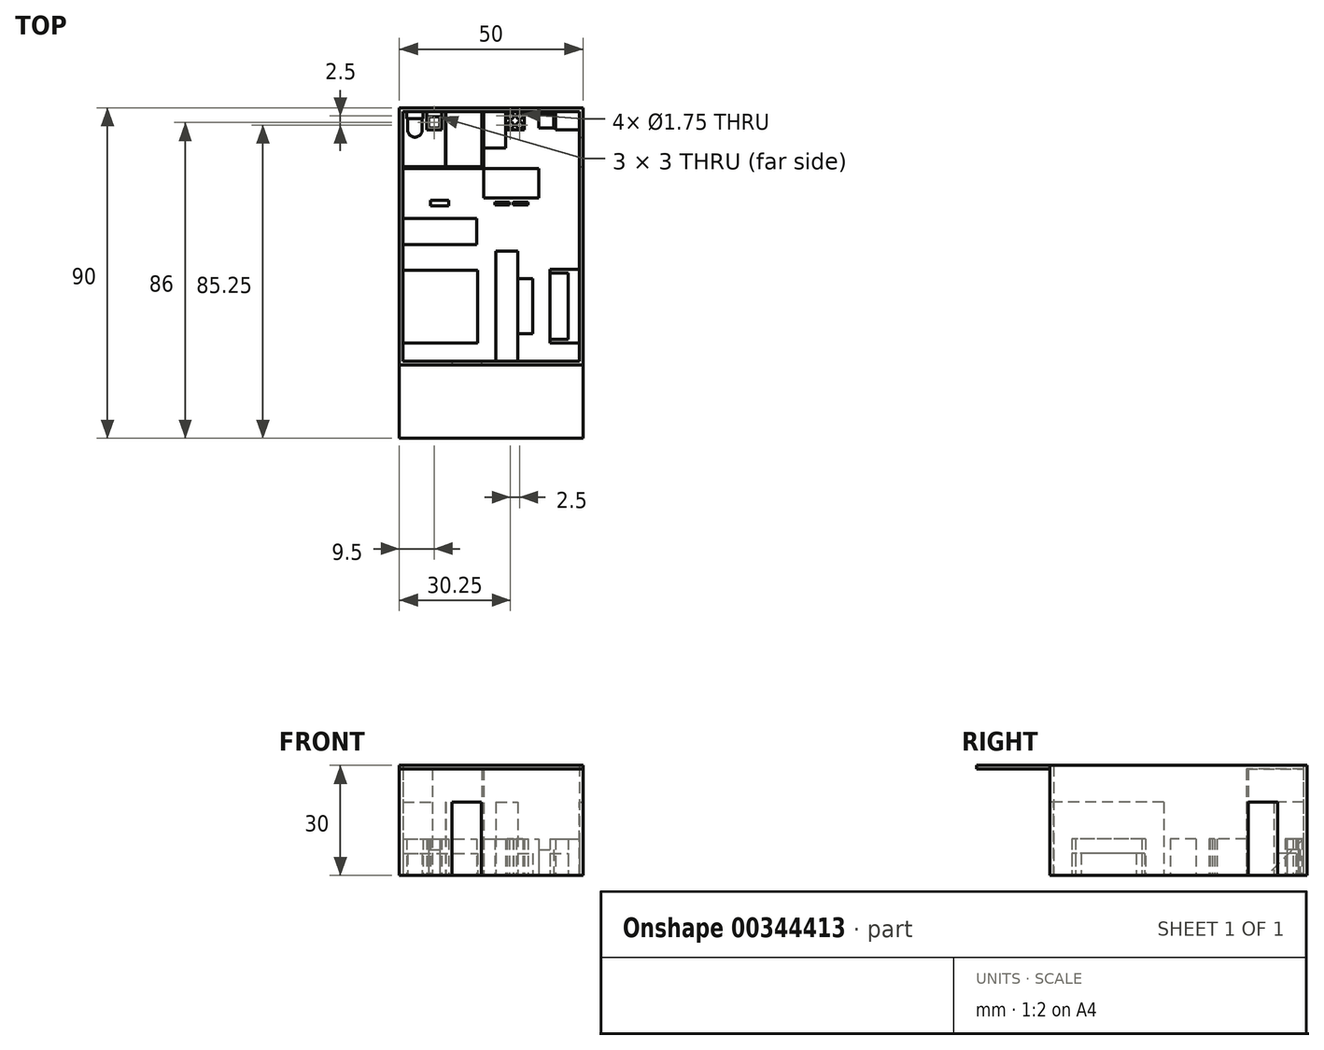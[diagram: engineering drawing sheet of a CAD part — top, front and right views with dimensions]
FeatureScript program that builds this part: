
annotation { "Feature Type Name" : "Feature", "Feature Type Description" : "" }
export const myFeature = defineFeature(function(context is Context, id is Id, definition is map)
    precondition{}
    {
        {
            var Q0;
            Q0=qCreatedBy(makeId("Top.planeOp"),FACE);
            var sketch = newSketch(context, id + "F0", { "sketchPlane" : qUnion([Q0])});
            skLineSegment(sketch, "E0.bottom", {"start": v(-25, 35) * mm, "end": v(25, 35) * mm});
            skLineSegment(sketch, "E0.top", {"start": v(-25, -35) * mm, "end": v(25, -35) * mm});
            skLineSegment(sketch, "E0.left", {"start": v(-25, 35) * mm, "end": v(-25, -35) * mm});
            skLineSegment(sketch, "E0.right", {"start": v(25, 35) * mm, "end": v(25, -35) * mm});
            skLineSegment(sketch, "E1", {"start": v(-25, 0) * mm, "end": v(25, 0) * mm, "construction": true});
            skLineSegment(sketch, "E2", {"start": v(0, 35) * mm, "end": v(0, -35) * mm, "construction": true});
            skLineSegment(sketch, "E3", {"start": v(25, 35) * mm, "end": v(0, 0) * mm, "construction": true});
            skSolve(sketch);
        }
        {
            var Q0;
            Q0=makeQuery(id+"F0.imprint","IMPRINT",FACE,{"disambiguationData":[TD([[makeQuery(id+"F0.imprint","IMPRINT",EDGE,{"derivedFrom":sQuery(id+"F0.wireOp",EDGE,"E0.bottom")}),-1.0]])]});
            extrude(context, id + "F1", {"entities" : qUnion([Q0]), "depth" : 30 * mm});
        }
        {
            var Q0;
            Q0=makeQuery(id+"F1.opExtrude","CAP_FACE",FACE,{"disambiguationData":[OSD([sQuery(id+"F0.wireOp",EDGE,"E0.bottom"),sQuery(id+"F0.wireOp",EDGE,"E0.top"),sQuery(id+"F0.wireOp",EDGE,"E0.left"),sQuery(id+"F0.wireOp",EDGE,"E0.right")])],"isStart":false});
            var Q1;
            Q1=makeQuery(id+"F1.opExtrude","CAP_FACE",FACE,{"disambiguationData":[OSD([sQuery(id+"F0.wireOp",EDGE,"E0.bottom"),sQuery(id+"F0.wireOp",EDGE,"E0.top"),sQuery(id+"F0.wireOp",EDGE,"E0.left"),sQuery(id+"F0.wireOp",EDGE,"E0.right")])],"isStart":true});
            shell(context, id + "F2", {"entities" : qUnion([Q0, Q1]), "thickness" : 1 * mm});
        }
        {
            var Q0;
            Q0=qCreatedBy(makeId("Top.planeOp"),FACE);
            var sketch = newSketch(context, id + "F3", { "sketchPlane" : qUnion([Q0])});
            skLineSegment(sketch, "E4.right", {"start": v(4, 34) * mm, "end": v(4, 29) * mm});
            skLineSegment(sketch, "E5.bottom", {"start": v(4, 34) * mm, "end": v(9, 34) * mm});
            skLineSegment(sketch, "E5.top", {"start": v(4, 29) * mm, "end": v(9, 29) * mm});
            skLineSegment(sketch, "E5.right", {"start": v(9, 34) * mm, "end": v(9, 29) * mm});
            skLineSegment(sketch, "E6.bottom", {"start": v(16, -9) * mm, "end": v(24, -9) * mm});
            skLineSegment(sketch, "E6.top", {"start": v(16, -29) * mm, "end": v(24, -29) * mm});
            skLineSegment(sketch, "E6.left", {"start": v(16, -9) * mm, "end": v(16, -29) * mm});
            skLineSegment(sketch, "E6.right", {"start": v(24, -9) * mm, "end": v(24, -29) * mm});
            skLineSegment(sketch, "E7.bottom", {"start": v(16, -10) * mm, "end": v(21, -10) * mm});
            skLineSegment(sketch, "E7.top", {"start": v(16, -28) * mm, "end": v(21, -28) * mm});
            skLineSegment(sketch, "E7.left", {"start": v(16, -10) * mm, "end": v(16, -28) * mm});
            skLineSegment(sketch, "E7.right", {"start": v(21, -10) * mm, "end": v(21, -28) * mm});
            skLineSegment(sketch, "E8.bottom", {"start": v(7.3, -11.5) * mm, "end": v(11.3, -11.5) * mm});
            skLineSegment(sketch, "E8.top", {"start": v(7.3, -26.5) * mm, "end": v(11.3, -26.5) * mm});
            skLineSegment(sketch, "E8.left", {"start": v(7.3, -11.5) * mm, "end": v(7.3, -26.5) * mm});
            skLineSegment(sketch, "E8.right", {"start": v(11.3, -11.5) * mm, "end": v(11.3, -26.5) * mm});
            skLineSegment(sketch, "E9.bottom", {"start": v(1.3, -4) * mm, "end": v(7.3, -4) * mm});
            skLineSegment(sketch, "E9.top", {"start": v(1.3, -34) * mm, "end": v(7.3, -34) * mm});
            skLineSegment(sketch, "E9.left", {"start": v(1.3, -4) * mm, "end": v(1.3, -34) * mm});
            skLineSegment(sketch, "E9.right", {"start": v(7.3, -4) * mm, "end": v(7.3, -34) * mm});
            skLineSegment(sketch, "E10.bottom", {"start": v(-24, -9.2) * mm, "end": v(-3.7, -9.2) * mm});
            skLineSegment(sketch, "E10.top", {"start": v(-24, -29) * mm, "end": v(-3.7, -29) * mm});
            skLineSegment(sketch, "E10.left", {"start": v(-24, -9.2) * mm, "end": v(-24, -29) * mm});
            skLineSegment(sketch, "E10.right", {"start": v(-3.7, -9.2) * mm, "end": v(-3.7, -29) * mm});
            skLineSegment(sketch, "E11.bottom", {"start": v(-24, 4.8) * mm, "end": v(-4, 4.8) * mm});
            skLineSegment(sketch, "E11.top", {"start": v(-24, -2.2) * mm, "end": v(-4, -2.2) * mm});
            skLineSegment(sketch, "E11.left", {"start": v(-24, 4.8) * mm, "end": v(-24, -2.2) * mm});
            skLineSegment(sketch, "E11.right", {"start": v(-4, 4.8) * mm, "end": v(-4, -2.2) * mm});
            skLineSegment(sketch, "E12.bottom", {"start": v(-16.5, 9.8) * mm, "end": v(-11.5, 9.8) * mm});
            skLineSegment(sketch, "E12.top", {"start": v(-16.5, 4.8) * mm, "end": v(-11.5, 4.8) * mm});
            skLineSegment(sketch, "E12.left", {"start": v(-16.5, 9.8) * mm, "end": v(-16.5, 4.8) * mm});
            skLineSegment(sketch, "E12.right", {"start": v(-11.5, 9.8) * mm, "end": v(-11.5, 4.8) * mm});
            skLineSegment(sketch, "E13.bottom", {"start": v(-24, -29) * mm, "end": v(-19, -29) * mm});
            skLineSegment(sketch, "E13.top", {"start": v(-24, -34) * mm, "end": v(-19, -34) * mm});
            skLineSegment(sketch, "E13.left", {"start": v(-24, -29) * mm, "end": v(-24, -34) * mm});
            skLineSegment(sketch, "E13.right", {"start": v(-19, -29) * mm, "end": v(-19, -34) * mm});
            skLineSegment(sketch, "E14", {"start": v(-16.5, 8.3) * mm, "end": v(-11.5, 8.3) * mm});
            skLineSegment(sketch, "E15", {"start": v(-14, 4.8) * mm, "end": v(-14, 9.8) * mm, "construction": true});
            skLineSegment(sketch, "E16", {"start": v(-14, -2.2) * mm, "end": v(-14, 4.8) * mm, "construction": true});
            skLineSegment(sketch, "E17.top", {"start": v(-23, 32) * mm, "end": v(-18.5, 32) * mm});
            skLineSegment(sketch, "E17.left", {"start": v(-23, 34) * mm, "end": v(-23, 32) * mm});
            skLineSegment(sketch, "E17.right", {"start": v(-18.5, 34) * mm, "end": v(-18.5, 32) * mm});
            skLineSegment(sketch, "E18", {"start": v(-22.75, 32) * mm, "end": v(-22.75, 29) * mm});
            skLineSegment(sketch, "E19", {"start": v(-18.75, 32) * mm, "end": v(-18.75, 29) * mm});
            skLineSegment(sketch, "E20", {"start": v(-22.75, 29) * mm, "end": v(-18.75, 29) * mm, "construction": true});
            skArc(sketch, "E21", {"start": v(-22.75, 29) * mm, "mid": v(-20.75, 27) * mm, "end": v(-18.75, 29) * mm});
            skLineSegment(sketch, "E22.top", {"start": v(-17.5, 29) * mm, "end": v(-13.5, 29) * mm});
            skLineSegment(sketch, "E22.left", {"start": v(-17.5, 34) * mm, "end": v(-17.5, 29) * mm});
            skLineSegment(sketch, "E22.right", {"start": v(-13.5, 34) * mm, "end": v(-13.5, 29) * mm});
            skLineSegment(sketch, "E23.bottom", {"start": v(-17, 32.5) * mm, "end": v(-14, 32.5) * mm});
            skLineSegment(sketch, "E23.top", {"start": v(-17, 29.5) * mm, "end": v(-14, 29.5) * mm});
            skLineSegment(sketch, "E23.left", {"start": v(-17, 32.5) * mm, "end": v(-17, 29.5) * mm});
            skLineSegment(sketch, "E23.right", {"start": v(-14, 32.5) * mm, "end": v(-14, 29.5) * mm});
            skLineSegment(sketch, "E24.bottom", {"start": v(-12.5, 34) * mm, "end": v(-2.5, 34) * mm});
            skLineSegment(sketch, "E24.top", {"start": v(-12.5, 19) * mm, "end": v(-2.5, 19) * mm});
            skLineSegment(sketch, "E24.left", {"start": v(-12.5, 34) * mm, "end": v(-12.5, 19) * mm});
            skLineSegment(sketch, "E24.right", {"start": v(-2.5, 34) * mm, "end": v(-2.5, 19) * mm});
            skLineSegment(sketch, "E25", {"start": v(-24, 19) * mm, "end": v(-2.5, 19) * mm});
            skLineSegment(sketch, "E26", {"start": v(-24, 18.5) * mm, "end": v(-2, 18.5) * mm});
            skLineSegment(sketch, "E27", {"start": v(-2, 18.5) * mm, "end": v(-2, 34) * mm});
            skLineSegment(sketch, "E28", {"start": v(-16, 19) * mm, "end": v(-16, 18.5) * mm});
            skLineSegment(sketch, "E29", {"start": v(-23, 34) * mm, "end": v(-18.5, 34) * mm});
            skLineSegment(sketch, "E30", {"start": v(-17.5, 34) * mm, "end": v(-13.5, 34) * mm});
            skLineSegment(sketch, "E31", {"start": v(-24, 19) * mm, "end": v(-24, 18.5) * mm});
            skLineSegment(sketch, "E32", {"start": v(-2.5, 34) * mm, "end": v(-2, 34) * mm});
            skLineSegment(sketch, "E33", {"start": v(1.3, -19) * mm, "end": v(24, -19) * mm, "construction": true});
            skPoint(sketch, "E33.endSnap0", {"position": v(7.3, -19) * mm});
            skLineSegment(sketch, "E34", {"start": v(24, -19) * mm, "end": v(16, -19) * mm, "construction": true});
            skLineSegment(sketch, "E35", {"start": v(7.3, -19) * mm, "end": v(11.3, -19) * mm, "construction": true});
            skLineSegment(sketch, "E36", {"start": v(6.5, 34) * mm, "end": v(6.5, 29) * mm, "construction": true});
            skLineSegment(sketch, "E37", {"start": v(6.5, 29) * mm, "end": v(4, 31.5) * mm, "construction": true});
            skLineSegment(sketch, "E38", {"start": v(4, 31.5) * mm, "end": v(6.5, 34) * mm, "construction": true});
            skLineSegment(sketch, "E39", {"start": v(4, 31.5) * mm, "end": v(9, 31.5) * mm, "construction": true});
            skLineSegment(sketch, "E40", {"start": v(9, 31.5) * mm, "end": v(6.5, 29) * mm, "construction": true});
            skLineSegment(sketch, "E41", {"start": v(6.5, 34) * mm, "end": v(9, 31.5) * mm, "construction": true});
            skLineSegment(sketch, "E42", {"start": v(4, 34) * mm, "end": v(9, 29) * mm, "construction": true});
            skLineSegment(sketch, "E43", {"start": v(9, 34) * mm, "end": v(4, 29) * mm, "construction": true});
            skCircle(sketch, "E44", {"center": v(5.25, 32.75) * mm, "radius": 0.87 * mm});
            skCircle(sketch, "E45", {"center": v(7.75, 32.75) * mm, "radius": 0.88 * mm});
            skCircle(sketch, "E46", {"center": v(5.25, 30.25) * mm, "radius": 0.88 * mm});
            skCircle(sketch, "E47", {"center": v(7.75, 30.25) * mm, "radius": 0.88 * mm});
            skLineSegment(sketch, "E48.bottom", {"start": v(-2, 34) * mm, "end": v(4, 34) * mm});
            skLineSegment(sketch, "E48.top", {"start": v(-2, 24) * mm, "end": v(4, 24) * mm});
            skLineSegment(sketch, "E48.left", {"start": v(-2, 34) * mm, "end": v(-2, 24) * mm});
            skLineSegment(sketch, "E48.right", {"start": v(4, 34) * mm, "end": v(4, 24) * mm});
            skLineSegment(sketch, "E49.bottom", {"start": v(9, 34) * mm, "end": v(24, 34) * mm});
            skLineSegment(sketch, "E49.top", {"start": v(9, 29) * mm, "end": v(24, 29) * mm});
            skLineSegment(sketch, "E49.right", {"start": v(24, 34) * mm, "end": v(24, 29) * mm});
            skLineSegment(sketch, "E50.bottom", {"start": v(13, 33) * mm, "end": v(17, 33) * mm});
            skLineSegment(sketch, "E50.top", {"start": v(13, 29.5) * mm, "end": v(17, 29.5) * mm});
            skLineSegment(sketch, "E50.left", {"start": v(13, 33) * mm, "end": v(13, 29.5) * mm});
            skLineSegment(sketch, "E50.right", {"start": v(17, 33) * mm, "end": v(17, 29.5) * mm});
            skLineSegment(sketch, "E51.bottom", {"start": v(24, 34) * mm, "end": v(17.5, 34) * mm});
            skLineSegment(sketch, "E51.top", {"start": v(24, 29) * mm, "end": v(17.5, 29) * mm});
            skLineSegment(sketch, "E51.right", {"start": v(17.5, 34) * mm, "end": v(17.5, 29) * mm});
            skLineSegment(sketch, "E52.bottom", {"start": v(-2, 18.5) * mm, "end": v(13, 18.5) * mm});
            skLineSegment(sketch, "E52.top", {"start": v(-2, 10.5) * mm, "end": v(13, 10.5) * mm});
            skLineSegment(sketch, "E52.left", {"start": v(-2, 18.5) * mm, "end": v(-2, 10.5) * mm});
            skLineSegment(sketch, "E52.right", {"start": v(13, 18.5) * mm, "end": v(13, 10.5) * mm});
            skLineSegment(sketch, "E53.bottom", {"start": v(1, 10.5) * mm, "end": v(5, 10.5) * mm});
            skLineSegment(sketch, "E53.top", {"start": v(1, 8.5) * mm, "end": v(5, 8.5) * mm});
            skLineSegment(sketch, "E53.left", {"start": v(1, 10.5) * mm, "end": v(1, 8.5) * mm});
            skLineSegment(sketch, "E53.right", {"start": v(5, 10.5) * mm, "end": v(5, 8.5) * mm});
            skLineSegment(sketch, "E54.bottom", {"start": v(6, 10.5) * mm, "end": v(10, 10.5) * mm});
            skLineSegment(sketch, "E54.top", {"start": v(6, 8.5) * mm, "end": v(10, 8.5) * mm});
            skLineSegment(sketch, "E54.left", {"start": v(6, 10.5) * mm, "end": v(6, 8.5) * mm});
            skLineSegment(sketch, "E54.right", {"start": v(10, 10.5) * mm, "end": v(10, 8.5) * mm});
            skLineSegment(sketch, "E55", {"start": v(1, 9.25) * mm, "end": v(5, 9.25) * mm});
            skLineSegment(sketch, "E56", {"start": v(6, 9.25) * mm, "end": v(10, 9.25) * mm});
            skLineSegment(sketch, "E57", {"start": v(-12.3, 34) * mm, "end": v(-12.3, 19) * mm});
            skLineSegment(sketch, "E58", {"start": v(-12.5, 26) * mm, "end": v(-12.3, 26) * mm});
            skSolve(sketch);
        }
        {
            var Q0;
            Q0=makeQuery(id+"F3.imprint","IMPRINT",FACE,{"disambiguationData":[TD([[makeQuery(id+"F3.imprint","IMPRINT",EDGE,{"derivedFrom":sQuery(id+"F3.wireOp",EDGE,"E22.top")}),1.0]])]});
            var Q1;
            {var subQ0=sQuery(id+"F3.wireOp",EDGE,"E17.left");Q1=makeQuery(id+"F3.imprint","IMPRINT",FACE,{"disambiguationData":[TD([[makeQuery(id+"F3.imprint","IMPRINT",EDGE,{"derivedFrom":subQ0}),1.0]])]});}
            var Q2;
            Q2=makeQuery(id+"F3.imprint","IMPRINT",FACE,{"disambiguationData":[TD([[makeQuery(id+"F3.imprint","IMPRINT",EDGE,{"derivedFrom":sQuery(id+"F3.wireOp",EDGE,"E52.bottom")}),-1.0]])]});
            var Q3;
            {var subQ0=sQuery(id+"F3.wireOp",EDGE,"E53.top");Q3=makeQuery(id+"F3.imprint","IMPRINT",FACE,{"disambiguationData":[TD([[makeQuery(id+"F3.imprint","IMPRINT",EDGE,{"derivedFrom":subQ0}),1.0]])]});}
            var Q4;
            {var subQ0=sQuery(id+"F3.wireOp",EDGE,"E54.top");Q4=makeQuery(id+"F3.imprint","IMPRINT",FACE,{"disambiguationData":[TD([[makeQuery(id+"F3.imprint","IMPRINT",EDGE,{"derivedFrom":subQ0}),1.0]])]});}
            var Q5;
            {var subQ0=sQuery(id+"F3.wireOp",EDGE,"E12.bottom");Q5=makeQuery(id+"F3.imprint","IMPRINT",FACE,{"disambiguationData":[TD([[makeQuery(id+"F3.imprint","IMPRINT",EDGE,{"derivedFrom":subQ0}),-1.0]])]});}
            var Q6;
            Q6=makeQuery(id+"F3.imprint","IMPRINT",FACE,{"disambiguationData":[TD([[makeQuery(id+"F3.imprint","IMPRINT",EDGE,{"derivedFrom":sQuery(id+"F3.wireOp",EDGE,"E11.top")}),1.0]])]});
            var Q7;
            Q7=makeQuery(id+"F3.imprint","IMPRINT",FACE,{"disambiguationData":[TD([[makeQuery(id+"F3.imprint","IMPRINT",EDGE,{"derivedFrom":sQuery(id+"F3.wireOp",EDGE,"E49.bottom")}),-1.0]])]});
            var Q8;
            Q8=makeQuery(id+"F3.imprint","IMPRINT",FACE,{"disambiguationData":[TD([[makeQuery(id+"F3.imprint","IMPRINT",EDGE,{"derivedFrom":sQuery(id+"F3.wireOp",EDGE,"E13.bottom")}),-1.0]])]});
            var Q9;
            {var subQ4=sQuery(id+"F3.wireOp",EDGE,"E6.bottom");Q9=makeQuery(id+"F3.imprint","IMPRINT",FACE,{"disambiguationData":[TD([[makeQuery(id+"F3.imprint","IMPRINT",EDGE,{"derivedFrom":subQ4}),-1.0]])]});}
            var Q10;
            {var subQ1=sQuery(id+"F3.wireOp",EDGE,"E5.bottom");Q10=makeQuery(id+"F3.imprint","IMPRINT",FACE,{"disambiguationData":[TD([[makeQuery(id+"F3.imprint","IMPRINT",EDGE,{"derivedFrom":subQ1}),-1.0]])]});}
            extrude(context, id + "F4", {"entities" : qUnion([Q0, Q1, Q2, Q3, Q4, Q5, Q6, Q7, Q8, Q9, Q10]), "operationType" : NewBodyOperationType.ADD, "depth" : 10 * mm});
        }
        {
            var Q0;
            {var subQ0=sQuery(id+"F3.wireOp",EDGE,"E12.top");Q0=makeQuery(id+"F3.imprint","IMPRINT",FACE,{"disambiguationData":[TD([[makeQuery(id+"F3.imprint","IMPRINT",EDGE,{"derivedFrom":subQ0}),1.0]])]});}
            var Q1;
            {var subQ0=sQuery(id+"F3.wireOp",EDGE,"E53.bottom");Q1=makeQuery(id+"F3.imprint","IMPRINT",FACE,{"disambiguationData":[TD([[makeQuery(id+"F3.imprint","IMPRINT",EDGE,{"derivedFrom":subQ0}),-1.0]])]});}
            var Q2;
            {var subQ0=sQuery(id+"F3.wireOp",EDGE,"E54.bottom");Q2=makeQuery(id+"F3.imprint","IMPRINT",FACE,{"disambiguationData":[TD([[makeQuery(id+"F3.imprint","IMPRINT",EDGE,{"derivedFrom":subQ0}),-1.0]])]});}
            var Q3;
            Q3=makeQuery(id+"F3.imprint","IMPRINT",FACE,{"disambiguationData":[TD([[makeQuery(id+"F3.imprint","IMPRINT",EDGE,{"derivedFrom":sQuery(id+"F3.wireOp",EDGE,"E7.bottom")}),-1.0]])]});
            var Q4;
            {var subQ0=sQuery(id+"F3.wireOp",EDGE,"E8.bottom");Q4=makeQuery(id+"F3.imprint","IMPRINT",FACE,{"disambiguationData":[TD([[makeQuery(id+"F3.imprint","IMPRINT",EDGE,{"derivedFrom":subQ0}),-1.0]])]});}
            var Q5;
            Q5=makeQuery(id+"F3.imprint","IMPRINT",FACE,{"disambiguationData":[TD([[makeQuery(id+"F3.imprint","IMPRINT",EDGE,{"derivedFrom":sQuery(id+"F3.wireOp",EDGE,"E10.bottom")}),-1.0]])]});
            var Q6;
            {var subQ0=sQuery(id+"F3.wireOp",EDGE,"E18");Q6=makeQuery(id+"F3.imprint","IMPRINT",FACE,{"disambiguationData":[TD([[makeQuery(id+"F3.imprint","IMPRINT",EDGE,{"derivedFrom":subQ0}),1.0]])]});}
            extrude(context, id + "F5", {"entities" : qUnion([Q0, Q1, Q2, Q3, Q4, Q5, Q6]), "depth" : 6 * mm});
        }
        {
            var Q0;
            {var subQ2=sQuery(id+"F3.wireOp",EDGE,"E9.bottom");Q0=makeQuery(id+"F3.imprint","IMPRINT",FACE,{"disambiguationData":[TD([[makeQuery(id+"F3.imprint","IMPRINT",EDGE,{"derivedFrom":subQ2}),-1.0]])]});}
            var Q1;
            Q1=makeQuery(id+"F3.imprint","IMPRINT",FACE,{"disambiguationData":[TD([[makeQuery(id+"F3.imprint","IMPRINT",EDGE,{"derivedFrom":sQuery(id+"F3.wireOp",EDGE,"E51.bottom")}),1.0]])]});
            var Q2;
            {var subQ3=sQuery(id+"F3.wireOp",EDGE,"E58");Q2=makeQuery(id+"F3.imprint","IMPRINT",FACE,{"disambiguationData":[TD([[makeQuery(id+"F3.imprint","IMPRINT",EDGE,{"derivedFrom":subQ3}),-1.0]])]});}
            extrude(context, id + "F6", {"entities" : qUnion([Q0, Q1, Q2]), "depth" : 20 * mm});
        }
        {
            var Q0;
            {var subQ5=sQuery(id+"F3.wireOp",EDGE,"E58");Q0=makeQuery(id+"F3.imprint","IMPRINT",FACE,{"disambiguationData":[TD([[makeQuery(id+"F3.imprint","IMPRINT",EDGE,{"derivedFrom":subQ5}),1.0]])]});}
            extrude(context, id + "F7", {"entities" : qUnion([Q0]), "depth" : 20 * mm});
        }
        {
            var Q0;
            {var subQ1=sQuery(id+"F3.wireOp",EDGE,"E48.bottom");Q0=makeQuery(id+"F3.imprint","IMPRINT",FACE,{"disambiguationData":[TD([[makeQuery(id+"F3.imprint","IMPRINT",EDGE,{"derivedFrom":subQ1}),-1.0]])]});}
            extrude(context, id + "F8", {"entities" : qUnion([Q0]), "depth" : 10 * mm});
        }
        {
            var Q0;
            Q0=makeQuery(id+"F8.opExtrude","CAP_EDGE",EDGE,{"disambiguationData":[OSD([sQuery(id+"F3.wireOp",EDGE,"E48.top")])],"isStart":false});
            chamfer(context, id + "F9", {"entities" : qUnion([Q0]), "width" : 10 * mm, "tangentPropagation" : true});
        }
        {
            var Q0;
            Q0=makeQuery(id+"F3.imprint","IMPRINT",FACE,{"disambiguationData":[TD([[makeQuery(id+"F3.imprint","IMPRINT",EDGE,{"derivedFrom":sQuery(id+"F3.wireOp",EDGE,"E23.bottom")}),-1.0]])]});
            var Q1;
            Q1=makeQuery(id+"F3.imprint","IMPRINT",FACE,{"disambiguationData":[TD([[makeQuery(id+"F3.imprint","IMPRINT",EDGE,{"derivedFrom":sQuery(id+"F3.wireOp",EDGE,"E50.bottom")}),-1.0]])]});
            extrude(context, id + "F10", {"entities" : qUnion([Q0, Q1]), "depth" : 7 * mm});
        }
        {
            var Q0;
            Q0=sQuery(id+"F3.wireOp",EDGE,"E47");
            var Q1;
            Q1=sQuery(id+"F3.wireOp",EDGE,"E45");
            var Q2;
            Q2=sQuery(id+"F3.wireOp",EDGE,"E44");
            var Q3;
            Q3=sQuery(id+"F3.wireOp",EDGE,"E46");
            extrude(context, id + "F11", {"bodyType" : ToolBodyType.SURFACE, "surfaceEntities" : qUnion([Q0, Q1, Q2, Q3]), "depth" : 11 * mm});
        }
        {
            var Q0;
            {var subQ1=sQuery(id+"F3.wireOp",EDGE,"E24.right");Q0=makeQuery(id+"F3.imprint","IMPRINT",FACE,{"disambiguationData":[TD([[makeQuery(id+"F3.imprint","IMPRINT",EDGE,{"derivedFrom":subQ1}),1.0]])]});}
            extrude(context, id + "F12", {"entities" : qUnion([Q0]), "depth" : 29 * mm});
        }
        {
            var Q0;
            {var subQ2=sQuery(id+"F3.wireOp",EDGE,"E28");Q0=makeQuery(id+"F3.imprint","IMPRINT",FACE,{"disambiguationData":[TD([[makeQuery(id+"F3.imprint","IMPRINT",EDGE,{"derivedFrom":subQ2}),-1.0]])]});}
            extrude(context, id + "F13", {"entities" : qUnion([Q0]), "depth" : 29 * mm});
        }
        {
            var Q0;
            {var subQ2=sQuery(id+"F3.wireOp",EDGE,"E28");Q0=makeQuery(id+"F3.imprint","IMPRINT",FACE,{"disambiguationData":[TD([[makeQuery(id+"F3.imprint","IMPRINT",EDGE,{"derivedFrom":subQ2}),-1.0]])]});}
            extrude(context, id + "F14", {"entities" : qUnion([Q0]), "operationType" : NewBodyOperationType.REMOVE, "depth" : 20 * mm});
        }
        {
            var Q0;
            {var subQ2=sQuery(id+"F3.wireOp",EDGE,"E28");Q0=makeQuery(id+"F3.imprint","IMPRINT",FACE,{"disambiguationData":[TD([[makeQuery(id+"F3.imprint","IMPRINT",EDGE,{"derivedFrom":subQ2}),-1.0]])]});}
            extrude(context, id + "F15", {"entities" : qUnion([Q0]), "depth" : 20 * mm});
        }
        {
            var Q0;
            Q0=makeQuery(id+"F1.opExtrude","CAP_FACE",FACE,{"disambiguationData":[OSD([sQuery(id+"F0.wireOp",EDGE,"E0.bottom"),sQuery(id+"F0.wireOp",EDGE,"E0.top"),sQuery(id+"F0.wireOp",EDGE,"E0.left"),sQuery(id+"F0.wireOp",EDGE,"E0.right")])],"isStart":false});
            var sketch = newSketch(context, id + "F16", { "sketchPlane" : qUnion([Q0])});
            skLineSegment(sketch, "E59.bottom", {"start": v(-25, -35) * mm, "end": v(25, -35) * mm});
            skLineSegment(sketch, "E59.top", {"start": v(-25, -55) * mm, "end": v(25, -55) * mm});
            skLineSegment(sketch, "E59.left", {"start": v(-25, -35) * mm, "end": v(-25, -55) * mm});
            skLineSegment(sketch, "E59.right", {"start": v(25, -35) * mm, "end": v(25, -55) * mm});
            skLineSegment(sketch, "E60.bottom", {"start": v(25, -35) * mm, "end": v(-25, -35) * mm});
            skLineSegment(sketch, "E60.top", {"start": v(25, 35) * mm, "end": v(-25, 35) * mm});
            skLineSegment(sketch, "E60.left", {"start": v(25, -35) * mm, "end": v(25, 35) * mm});
            skLineSegment(sketch, "E60.right", {"start": v(-25, -35) * mm, "end": v(-25, 35) * mm});
            skSolve(sketch);
        }
        {
            var Q0;
            Q0=makeQuery(id+"F16.imprint","IMPRINT",FACE,{"disambiguationData":[TD([[makeQuery(id+"F16.imprint","IMPRINT",EDGE,{"derivedFrom":sQuery(id+"F16.wireOp",EDGE,"E59.top")}),1.0]])]});
            extrude(context, id + "F17", {"entities" : qUnion([Q0]), "oppositeDirection" : true, "depth" : 1 * mm});
        }
        {
            var Q0;
            Q0=makeQuery(id+"F1.opExtrude","SWEPT_FACE",FACE,{"disambiguationData":[OSD([sQuery(id+"F0.wireOp",EDGE,"E0.right")])]});
            var sketch = newSketch(context, id + "F18", { "sketchPlane" : qUnion([Q0])});
            skLineSegment(sketch, "E61.bottom", {"start": v(19, 0) * mm, "end": v(27, 0) * mm});
            skLineSegment(sketch, "E61.top", {"start": v(19, 20) * mm, "end": v(27, 20) * mm});
            skLineSegment(sketch, "E61.left", {"start": v(19, 0) * mm, "end": v(19, 20) * mm});
            skLineSegment(sketch, "E61.right", {"start": v(27, 0) * mm, "end": v(27, 20) * mm});
            skSolve(sketch);
        }
        {
            var Q0;
            Q0=makeQuery(id+"F18.imprint","IMPRINT",FACE,{"disambiguationData":[TD([[makeQuery(id+"F18.imprint","IMPRINT",EDGE,{"derivedFrom":sQuery(id+"F18.wireOp",EDGE,"E61.bottom")}),-1.0]])]});
            extrude(context, id + "F19", {"entities" : qUnion([Q0]), "operationType" : NewBodyOperationType.REMOVE, "oppositeDirection" : true, "depth" : 1 * mm});
        }
        {
            var Q0;
            Q0=makeQuery(id+"F18.imprint","IMPRINT",FACE,{"disambiguationData":[TD([[makeQuery(id+"F18.imprint","IMPRINT",EDGE,{"derivedFrom":sQuery(id+"F18.wireOp",EDGE,"E61.bottom")}),-1.0]])]});
            extrude(context, id + "F20", {"entities" : qUnion([Q0]), "oppositeDirection" : true, "depth" : 1 * mm});
        }
        {
            var Q0;
            Q0=makeQuery(id+"F1.opExtrude","SWEPT_FACE",FACE,{"disambiguationData":[OSD([sQuery(id+"F0.wireOp",EDGE,"E0.top")])]});
            var sketch = newSketch(context, id + "F21", { "sketchPlane" : qUnion([Q0])});
            skLineSegment(sketch, "E62.bottom", {"start": v(-2.7, 0) * mm, "end": v(-10.7, 0) * mm});
            skLineSegment(sketch, "E62.top", {"start": v(-2.7, 20) * mm, "end": v(-10.7, 20) * mm});
            skLineSegment(sketch, "E62.left", {"start": v(-2.7, 0) * mm, "end": v(-2.7, 20) * mm});
            skLineSegment(sketch, "E62.right", {"start": v(-10.7, 0) * mm, "end": v(-10.7, 20) * mm});
            skSolve(sketch);
        }
        {
            var Q0;
            Q0=makeQuery(id+"F21.imprint","IMPRINT",FACE,{"disambiguationData":[TD([[makeQuery(id+"F21.imprint","IMPRINT",EDGE,{"derivedFrom":sQuery(id+"F21.wireOp",EDGE,"E62.bottom")}),1.0]])]});
            extrude(context, id + "F22", {"entities" : qUnion([Q0]), "operationType" : NewBodyOperationType.REMOVE, "oppositeDirection" : true, "depth" : 1 * mm});
        }
        {
            var Q0;
            Q0=makeQuery(id+"F21.imprint","IMPRINT",FACE,{"disambiguationData":[TD([[makeQuery(id+"F21.imprint","IMPRINT",EDGE,{"derivedFrom":sQuery(id+"F21.wireOp",EDGE,"E62.bottom")}),1.0]])]});
            extrude(context, id + "F23", {"entities" : qUnion([Q0]), "oppositeDirection" : true, "depth" : 1 * mm});
        }
    });
